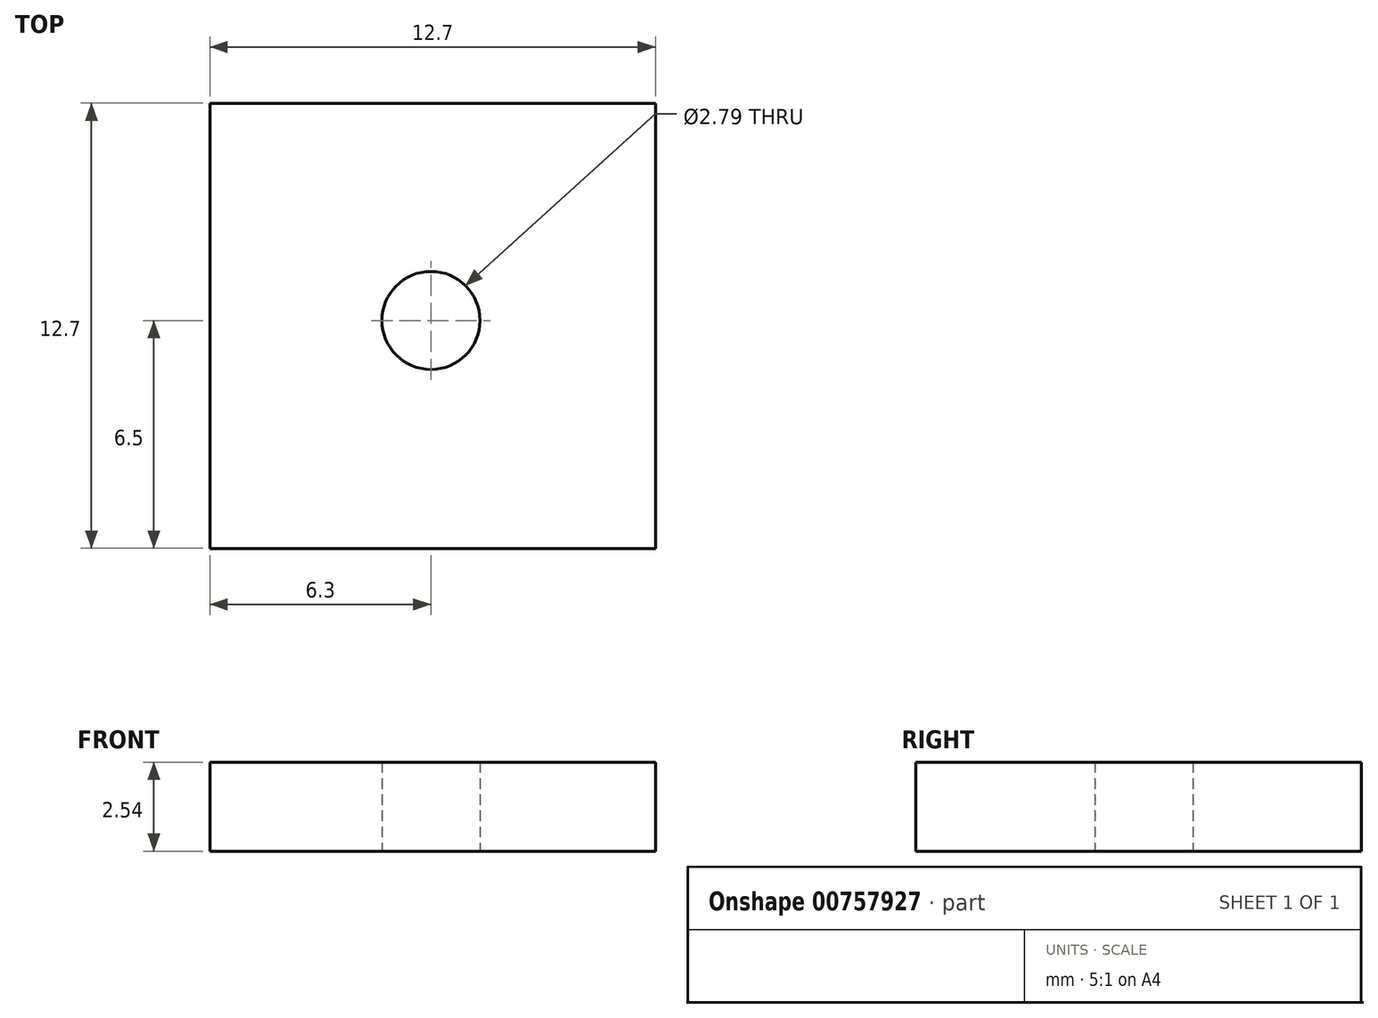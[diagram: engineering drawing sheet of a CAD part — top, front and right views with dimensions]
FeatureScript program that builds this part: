
annotation { "Feature Type Name" : "Feature", "Feature Type Description" : "" }
export const myFeature = defineFeature(function(context is Context, id is Id, definition is map)
    precondition{}
    {
        {
            var Q0;
            Q0=qCreatedBy(makeId("Top.planeOp"),FACE);
            var sketch = newSketch(context, id + "F0", { "sketchPlane" : qUnion([Q0])});
            skPoint(sketch, "E0.middle", {"position": v(0, 0) * mm});
            skCircle(sketch, "E1", {"center": v(0, 0) * mm, "radius": 1.4 * mm});
            skSolve(sketch);
        }
        {
            var Q0;
            Q0=qCreatedBy(makeId("Top.planeOp"),FACE);
            var sketch = newSketch(context, id + "F1", { "sketchPlane" : qUnion([Q0])});
            skLineSegment(sketch, "E2.bottom", {"start": v(6.4, 6.2) * mm, "end": v(-6.3, 6.2) * mm});
            skLineSegment(sketch, "E2.top", {"start": v(6.4, -6.5) * mm, "end": v(-6.3, -6.5) * mm});
            skLineSegment(sketch, "E2.left", {"start": v(6.4, 6.2) * mm, "end": v(6.4, -6.5) * mm});
            skLineSegment(sketch, "E2.right", {"start": v(-6.3, 6.2) * mm, "end": v(-6.3, -6.5) * mm});
            skSolve(sketch);
        }
        {
            var Q0;
            Q0 = qSketchRegion(id + "F1", true);
            extrude(context, id + "F2", {"entities" : qUnion([Q0]), "depth" : 2.54 * mm, "offsetDistance" : 25.4 * mm});
        }
        {
            var Q0;
            Q0 = qSketchRegion(id + "F0", true);
            extrude(context, id + "F3", {"entities" : qUnion([Q0]), "operationType" : NewBodyOperationType.REMOVE, "depth" : 22.7 * mm, "offsetDistance" : 25.4 * mm});
        }
    });
